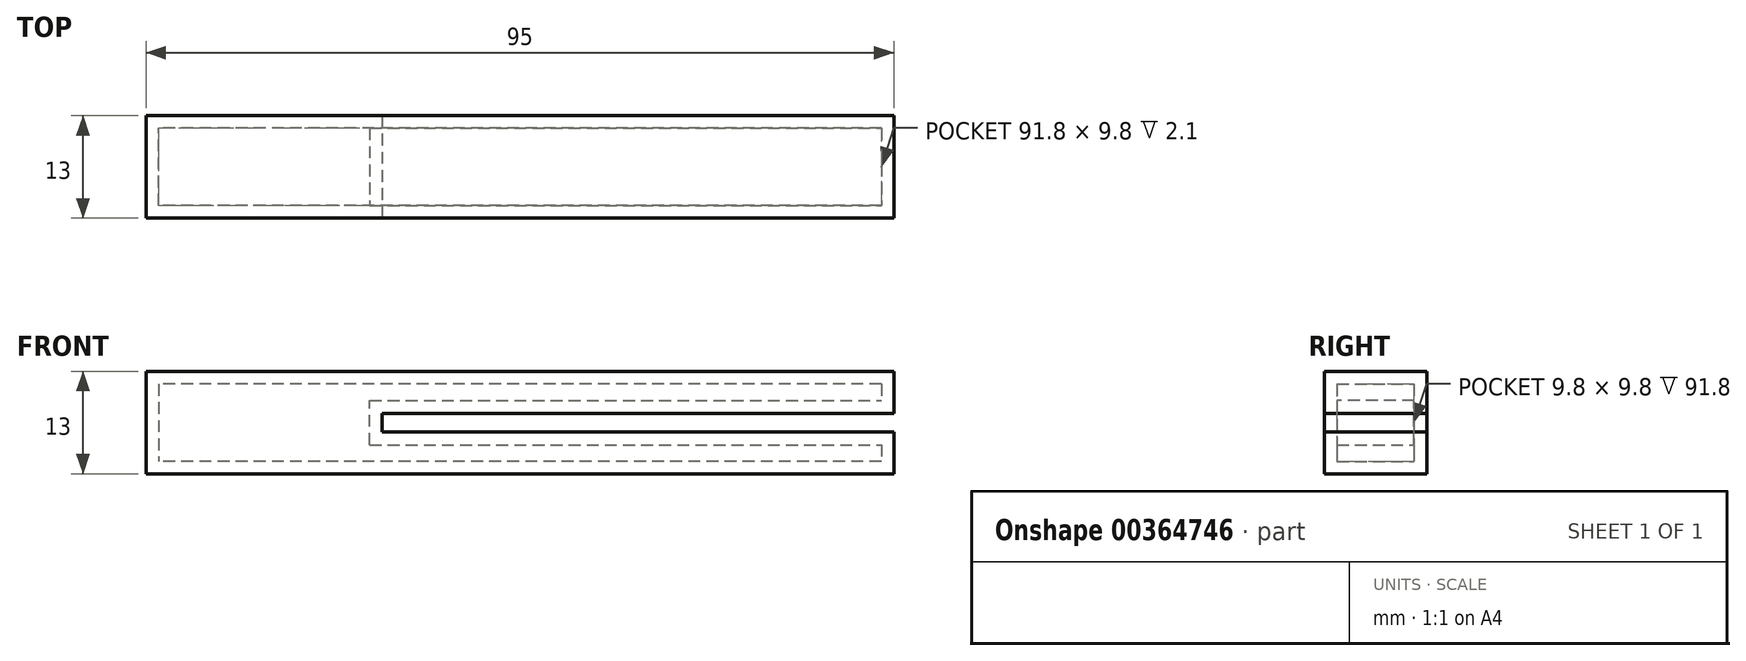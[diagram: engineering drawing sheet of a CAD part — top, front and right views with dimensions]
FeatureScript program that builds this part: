
annotation { "Feature Type Name" : "Feature", "Feature Type Description" : "" }
export const myFeature = defineFeature(function(context is Context, id is Id, definition is map)
    precondition{}
    {
        {
            var Q0;
            Q0=qCreatedBy(makeId("Right.planeOp"),FACE);
            var sketch = newSketch(context, id + "F0", { "sketchPlane" : qUnion([Q0])});
            skLineSegment(sketch, "E0.bottom", {"start": v(-6.5, 6.5) * mm, "end": v(6.5, 6.5) * mm});
            skLineSegment(sketch, "E0.top", {"start": v(-6.5, -6.5) * mm, "end": v(6.5, -6.5) * mm});
            skLineSegment(sketch, "E0.left", {"start": v(-6.5, 6.5) * mm, "end": v(-6.5, -6.5) * mm});
            skLineSegment(sketch, "E0.right", {"start": v(6.5, 6.5) * mm, "end": v(6.5, -6.5) * mm});
            skSolve(sketch);
        }
        {
            var Q0;
            Q0=qSketchRegion(id+"F0",true);
            extrude(context, id + "F1", {"entities" : qUnion([Q0]), "depth" : 95 * mm});
        }
        {
            var Q0;
            Q0=qCreatedBy(makeId("Right.planeOp"),FACE);
            cPlane(context, id + "F2", {"entities" : qUnion([Q0]), "cplaneType" : CPlaneType.OFFSET, "offset" : 110 * mm, "width" : 150 * mm, "height" : 150 * mm});
        }
        {
            var Q0;
            Q0=qCreatedBy(id+"F2.planeOp",FACE);
            var sketch = newSketch(context, id + "F3", { "sketchPlane" : qUnion([Q0])});
            skLineSegment(sketch, "E1", {"start": v(-6.5, 1.2) * mm, "end": v(-6.5, -1.2) * mm});
            skLineSegment(sketch, "E2", {"start": v(-6.5, -1.2) * mm, "end": v(6.5, -1.2) * mm});
            skLineSegment(sketch, "E3", {"start": v(6.5, -1.2) * mm, "end": v(6.5, 1.2) * mm});
            skLineSegment(sketch, "E4", {"start": v(6.5, 1.2) * mm, "end": v(-6.5, 1.2) * mm});
            skSolve(sketch);
        }
        {
            var Q0;
            Q0=makeQuery(id+"F3.imprint","IMPRINT",FACE,{"disambiguationData":[TD([[makeQuery(id+"F3.imprint","IMPRINT",EDGE,{"derivedFrom":sQuery(id+"F3.wireOp",EDGE,"E1")}),1.0]])]});
            extrude(context, id + "F4", {"entities" : qUnion([Q0]), "operationType" : NewBodyOperationType.REMOVE, "oppositeDirection" : true, "depth" : 80 * mm});
        }
        {
            var Q0;
            Q0=makeQuery(id+"F1.opExtrude","CAP_FACE",FACE,{"disambiguationData":[OSD([sQuery(id+"F0.wireOp",EDGE,"E0.bottom"),sQuery(id+"F0.wireOp",EDGE,"E0.top"),sQuery(id+"F0.wireOp",EDGE,"E0.left"),sQuery(id+"F0.wireOp",EDGE,"E0.right")])],"isStart":true});
            var Q1;
            Q1=makeQuery(id+"F1.opExtrude","SWEPT_BODY",BODY,{"disambiguationData":[OSD([sQuery(id+"F0.wireOp",EDGE,"E0.bottom"),sQuery(id+"F0.wireOp",EDGE,"E0.top"),sQuery(id+"F0.wireOp",EDGE,"E0.left"),sQuery(id+"F0.wireOp",EDGE,"E0.right")])]});
            shell(context, id + "F5", {"isHollow" : true, "entities" : qUnion([Q0]), "parts" : qUnion([Q1]), "thickness" : 1.6 * mm});
        }
    });
